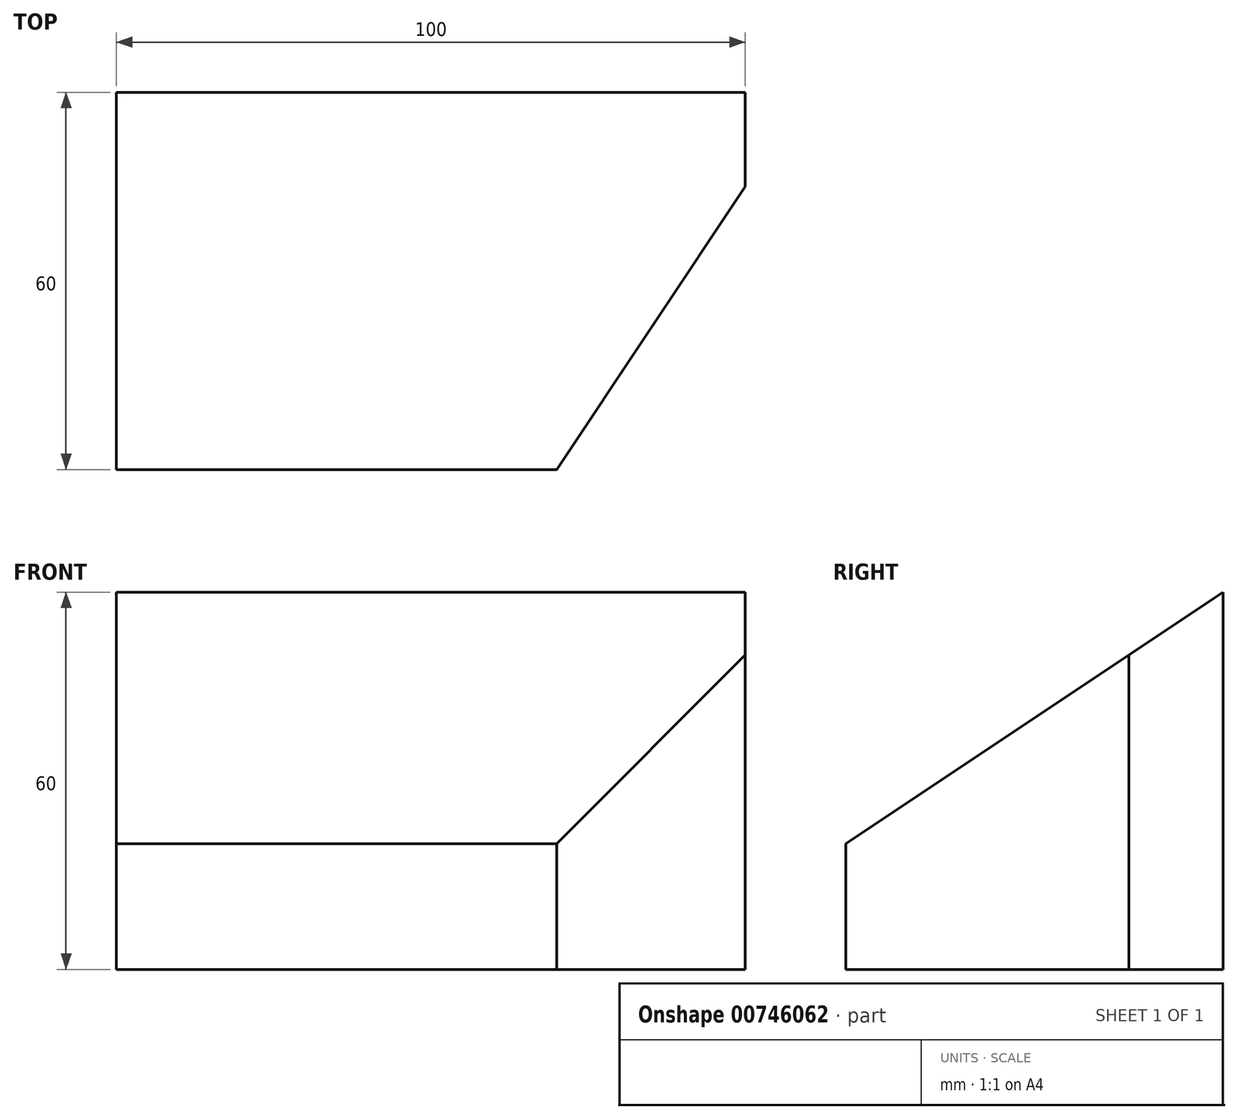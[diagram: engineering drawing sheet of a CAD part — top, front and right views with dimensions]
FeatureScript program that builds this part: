
annotation { "Feature Type Name" : "Feature", "Feature Type Description" : "" }
export const myFeature = defineFeature(function(context is Context, id is Id, definition is map)
    precondition{}
    {
        {
            var Q0;
            Q0=qCreatedBy(makeId("Front.planeOp"),FACE);
            var sketch = newSketch(context, id + "F0", { "sketchPlane" : qUnion([Q0])});
            skLineSegment(sketch, "E0", {"start": v(0, 0) * mm, "end": v(0, 20) * mm});
            skLineSegment(sketch, "E1", {"start": v(0, 20) * mm, "end": v(70, 20) * mm});
            skLineSegment(sketch, "E2", {"start": v(70, 20) * mm, "end": v(70, 0) * mm});
            skLineSegment(sketch, "E3", {"start": v(70, 0) * mm, "end": v(0, 0) * mm});
            skSolve(sketch);
        }
        {
            var Q0;
            Q0=makeQuery(id+"F0.imprint","IMPRINT",FACE,{"disambiguationData":[TD([[makeQuery(id+"F0.imprint","IMPRINT",EDGE,{"derivedFrom":sQuery(id+"F0.wireOp",EDGE,"E0")}),-1.0]])]});
            extrude(context, id + "F1", {"entities" : qUnion([Q0]), "depth" : 60 * mm, "offsetDistance" : 25 * mm});
        }
        {
            var Q0;
            Q0=makeQuery(id+"F1.opExtrude","SWEPT_FACE",FACE,{"disambiguationData":[OSD([sQuery(id+"F0.wireOp",EDGE,"E1")])]});
            var sketch = newSketch(context, id + "F2", { "sketchPlane" : qUnion([Q0])});
            skLineSegment(sketch, "E4", {"start": v(0, 0) * mm, "end": v(100, 0) * mm});
            skLineSegment(sketch, "E5", {"start": v(100, 0) * mm, "end": v(100, -15) * mm});
            skLineSegment(sketch, "E6", {"start": v(100, -15) * mm, "end": v(70, -60) * mm});
            skSolve(sketch);
        }
        {
            var Q0;
            {var subQ2=sQuery(id+"F2.wireOp",EDGE,"E5");Q0=makeQuery(id+"F2.imprint","IMPRINT",FACE,{"disambiguationData":[TD([[makeQuery(id+"F2.imprint","IMPRINT",EDGE,{"derivedFrom":subQ2}),-1.0]])]});}
            extrude(context, id + "F3", {"entities" : qUnion([Q0]), "operationType" : NewBodyOperationType.ADD, "oppositeDirection" : true, "depth" : 20 * mm, "offsetDistance" : 25 * mm});
        }
        {
            var Q0;
            Q0=makeQuery(id+"F1.opExtrude","SWEPT_FACE",FACE,{"disambiguationData":[OSD([sQuery(id+"F0.wireOp",EDGE,"E0")])]});
            var sketch = newSketch(context, id + "F4", { "sketchPlane" : qUnion([Q0])});
            skLineSegment(sketch, "E7", {"start": v(0, 0) * mm, "end": v(0, 60) * mm});
            skLineSegment(sketch, "E8", {"start": v(0, 60) * mm, "end": v(60, 20) * mm});
            skSolve(sketch);
        }
        {
            var Q0;
            {var subQ2=sQuery(id+"F4.wireOp",EDGE,"E8");Q0=makeQuery(id+"F4.imprint","IMPRINT",FACE,{"disambiguationData":[TD([[makeQuery(id+"F4.imprint","IMPRINT",EDGE,{"derivedFrom":subQ2}),-1.0]])]});}
            extrude(context, id + "F5", {"entities" : qUnion([Q0]), "operationType" : NewBodyOperationType.ADD, "oppositeDirection" : true, "depth" : 70 * mm, "offsetDistance" : 25 * mm});
        }
        {
            var Q0;
            {var subQ0=sQuery(id+"F0.wireOp",EDGE,"E1");Q0=makeQuery(id+"F3.boolean.opBoolean","MERGE",FACE,{"derivedFrom":[makeQuery(id+"F1.opExtrude","SWEPT_FACE",FACE,{"disambiguationData":[OSD([subQ0])]}),makeQuery(id+"F3.opExtrude","CAP_FACE",FACE,{"disambiguationData":[OSD([subQ0,sQuery(id+"F0.wireOp",EDGE,"E2"),sQuery(id+"F2.wireOp",EDGE,"E4"),sQuery(id+"F2.wireOp",EDGE,"E5"),sQuery(id+"F2.wireOp",EDGE,"E6")])],"isStart":true})]});}
            extrude(context, id + "F6", {"entities" : qUnion([Q0]), "operationType" : NewBodyOperationType.ADD, "depth" : 40 * mm, "offsetDistance" : 25 * mm});
        }
        {
            var Q0;
            Q0=makeQuery(id+"F6.opExtrude","SWEPT_FACE",FACE,{"disambiguationData":[OSD([sQuery(id+"F0.wireOp",EDGE,"E0"),sQuery(id+"F0.wireOp",EDGE,"E1")])]});
            extrude(context, id + "F7", {"entities" : qUnion([Q0]), "operationType" : NewBodyOperationType.REMOVE, "endBound" : BoundingType.THROUGH_ALL, "oppositeDirection" : true, "depth" : 25 * mm, "offsetDistance" : 25 * mm});
        }
    });
